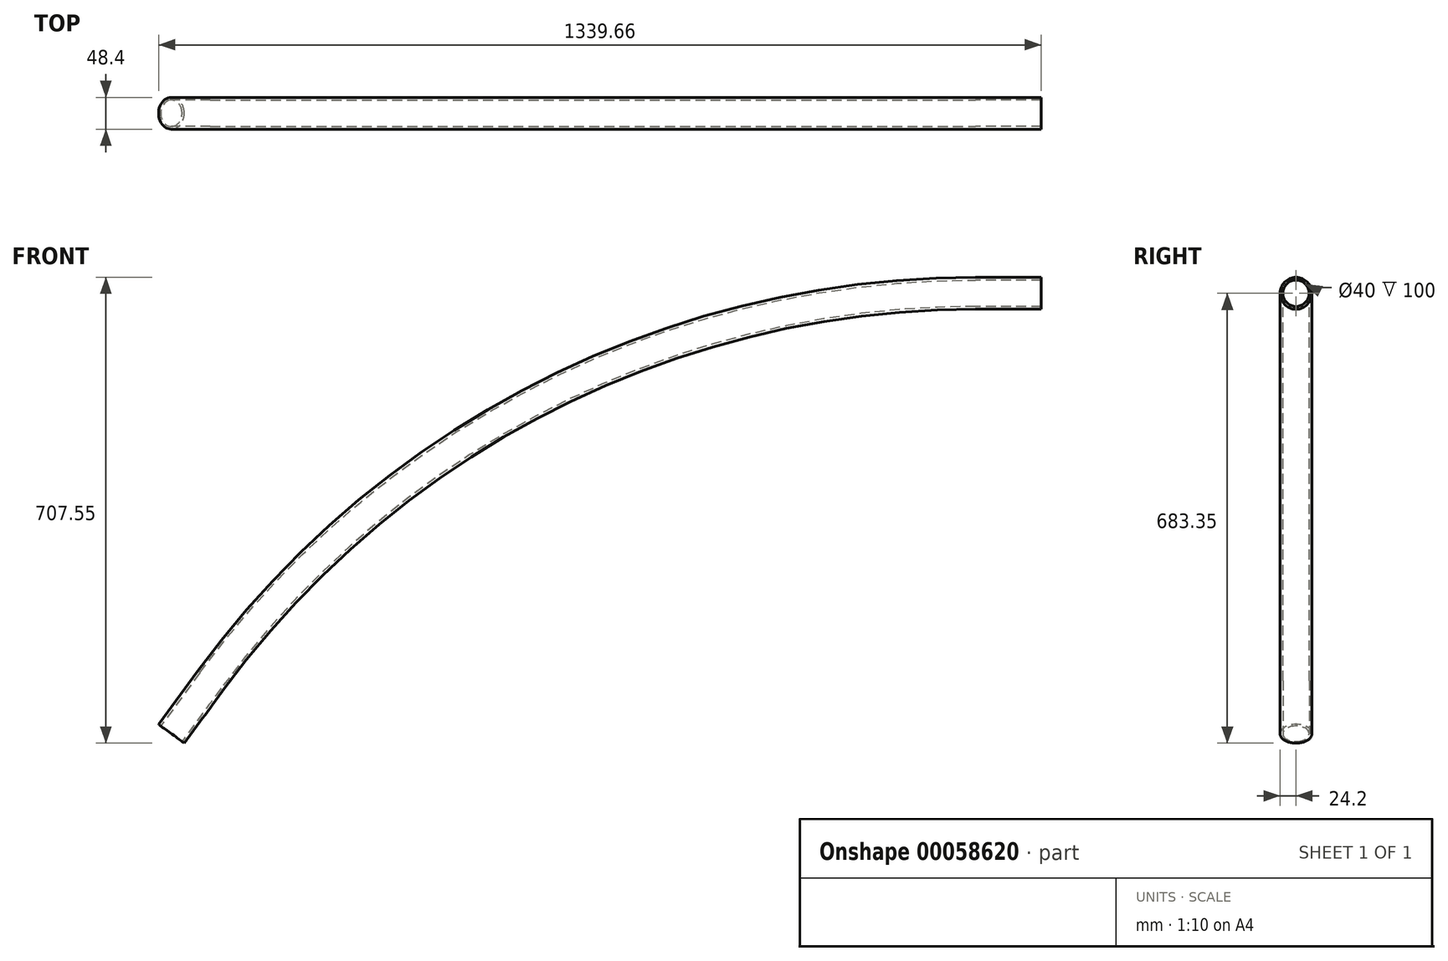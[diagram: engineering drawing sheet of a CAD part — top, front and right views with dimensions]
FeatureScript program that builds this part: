
annotation { "Feature Type Name" : "Feature", "Feature Type Description" : "" }
export const myFeature = defineFeature(function(context is Context, id is Id, definition is map)
    precondition{}
    {
        {
            var Q0;
            Q0=qCreatedBy(makeId("Right.planeOp"),FACE);
            var sketch = newSketch(context, id + "F0", { "sketchPlane" : qUnion([Q0])});
            skCircle(sketch, "E0", {"center": v(0, 0) * mm, "radius": 24.2 * mm});
            skCircle(sketch, "E1", {"center": v(0, 0) * mm, "radius": 20 * mm});
            skSolve(sketch);
        }
        {
            var Q0;
            Q0=qCreatedBy(makeId("Front.planeOp"),FACE);
            var sketch = newSketch(context, id + "F1", { "sketchPlane" : qUnion([Q0])});
            skLineSegment(sketch, "E2", {"start": v(0, 0) * mm, "end": v(-100, 0) * mm});
            skArc(sketch, "E3", {"start": v(-100, 0) * mm, "mid": v(-750.8, -155.5) * mm, "end": v(-1261.02, -588.4) * mm});
            skLineSegment(sketch, "E4", {"start": v(-1261.02, -588.4) * mm, "end": v(-1320.15, -669.04) * mm});
            skSolve(sketch);
        }
        {
            var Q0;
            Q0=makeQuery(id+"F0.imprint","IMPRINT",FACE,{"disambiguationData":[TD([[makeQuery(id+"F0.imprint","IMPRINT",EDGE,{"derivedFrom":sQuery(id+"F0.wireOp",EDGE,"E0")}),1.0]])]});
            var Q1;
            Q1=sQuery(id+"F1.wireOp",EDGE,"E2");
            var Q2;
            Q2=sQuery(id+"F1.wireOp",EDGE,"E3");
            var Q3;
            Q3=sQuery(id+"F1.wireOp",EDGE,"E4");
            sweep(context, id + "F2", {"profiles" : qUnion([Q0]), "path" : qUnion([Q1, Q2, Q3])});
        }
    });
